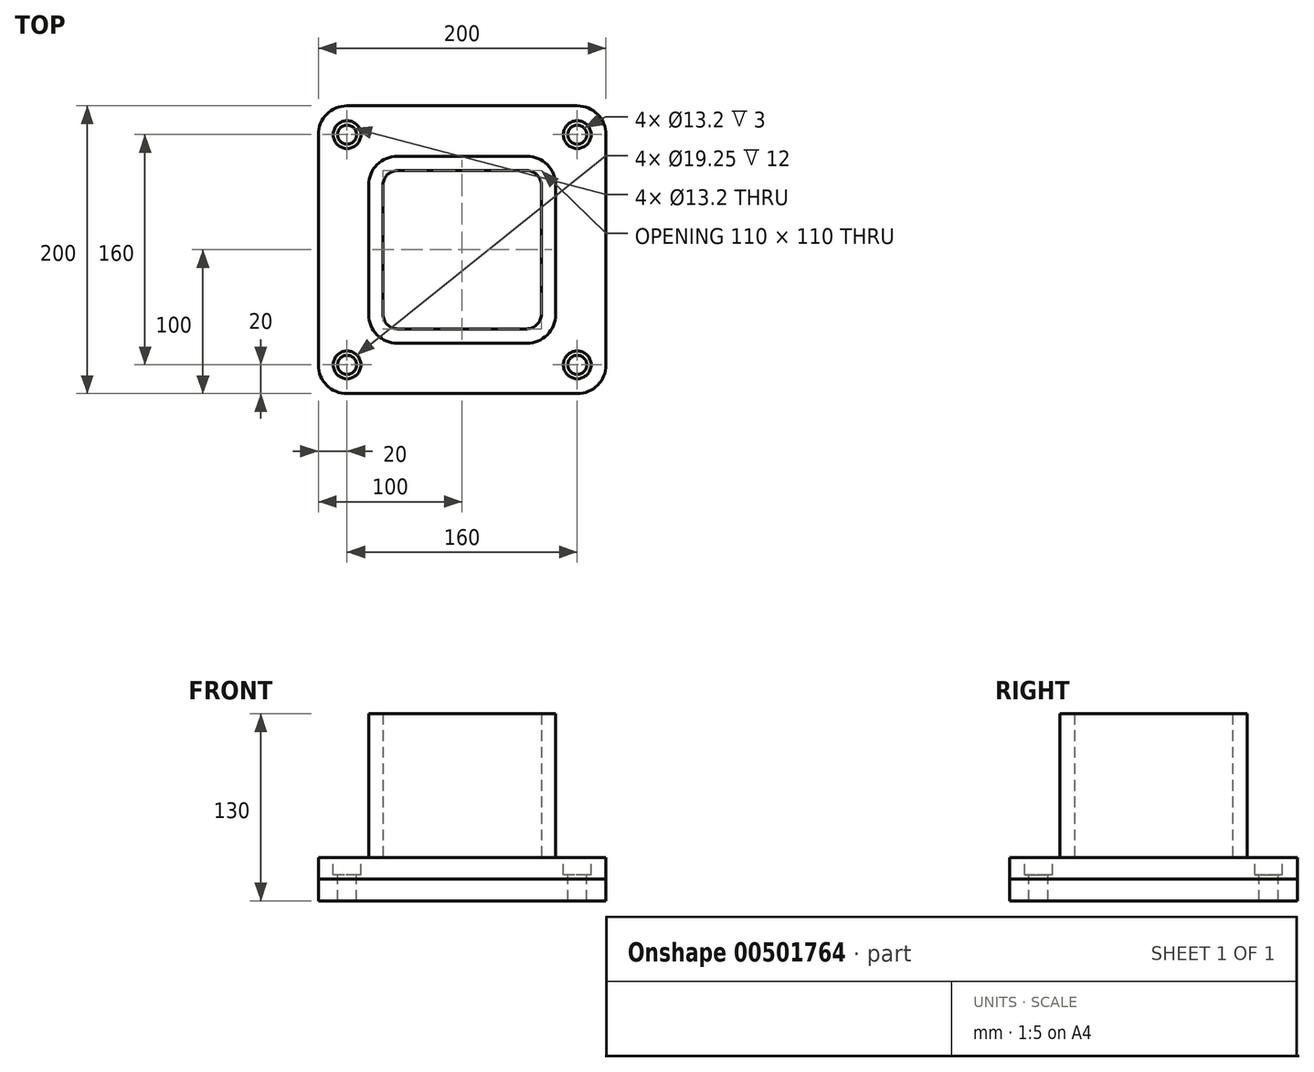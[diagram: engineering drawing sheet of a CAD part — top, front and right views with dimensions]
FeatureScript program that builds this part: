
annotation { "Feature Type Name" : "Feature", "Feature Type Description" : "" }
export const myFeature = defineFeature(function(context is Context, id is Id, definition is map)
    precondition{}
    {
        {
            var Q0;
            Q0=qCreatedBy(makeId("Top.planeOp"),FACE);
            var sketch = newSketch(context, id + "F0", { "sketchPlane" : qUnion([Q0])});
            skLineSegment(sketch, "E0.bottom", {"start": v(100, -100) * mm, "end": v(-100, -100) * mm});
            skLineSegment(sketch, "E0.top", {"start": v(100, 100) * mm, "end": v(-100, 100) * mm});
            skLineSegment(sketch, "E0.left", {"start": v(100, -100) * mm, "end": v(100, 100) * mm});
            skLineSegment(sketch, "E0.right", {"start": v(-100, -100) * mm, "end": v(-100, 100) * mm});
            skPoint(sketch, "E0.middle", {"position": v(0, 0) * mm});
            skSolve(sketch);
        }
        {
            var Q0;
            Q0=makeQuery(id+"F0.imprint","IMPRINT",FACE,{"disambiguationData":[TD([[makeQuery(id+"F0.imprint","IMPRINT",EDGE,{"derivedFrom":sQuery(id+"F0.wireOp",EDGE,"E0.bottom")}),-1.0]])]});
            extrude(context, id + "F1", {"entities" : qUnion([Q0]), "depth" : 15 * mm});
        }
        {
            var Q0;
            Q0=makeQuery(id+"F1.opExtrude","SWEPT_EDGE",EDGE,{"disambiguationData":[OSD([sQuery(id+"F0.wireOp",EDGE,"E0.bottom"),sQuery(id+"F0.wireOp",EDGE,"E0.left")])]});
            var Q1;
            Q1=makeQuery(id+"F1.opExtrude","SWEPT_EDGE",EDGE,{"disambiguationData":[OSD([sQuery(id+"F0.wireOp",EDGE,"E0.top"),sQuery(id+"F0.wireOp",EDGE,"E0.left")])]});
            var Q2;
            Q2=makeQuery(id+"F1.opExtrude","SWEPT_EDGE",EDGE,{"disambiguationData":[OSD([sQuery(id+"F0.wireOp",EDGE,"E0.bottom"),sQuery(id+"F0.wireOp",EDGE,"E0.right")])]});
            var Q3;
            Q3=makeQuery(id+"F1.opExtrude","SWEPT_EDGE",EDGE,{"disambiguationData":[OSD([sQuery(id+"F0.wireOp",EDGE,"E0.top"),sQuery(id+"F0.wireOp",EDGE,"E0.right")])]});
            fillet(context, id + "F2", {"entities" : qUnion([Q0, Q1, Q2, Q3]), "radius" : 20 * mm, "tangentPropagation" : true, "allowEdgeOverflow" : false});
        }
        {
            var Q0;
            Q0=makeQuery(id+"F1.opExtrude","CAP_FACE",FACE,{"disambiguationData":[OSD([sQuery(id+"F0.wireOp",EDGE,"E0.bottom"),sQuery(id+"F0.wireOp",EDGE,"E0.top"),sQuery(id+"F0.wireOp",EDGE,"E0.left"),sQuery(id+"F0.wireOp",EDGE,"E0.right")])],"isStart":false});
            var sketch = newSketch(context, id + "F3", { "sketchPlane" : qUnion([Q0])});
            skLineSegment(sketch, "E1.bottom", {"start": v(80, -80) * mm, "end": v(-80, -80) * mm});
            skLineSegment(sketch, "E1.top", {"start": v(80, 80) * mm, "end": v(-80, 80) * mm});
            skLineSegment(sketch, "E1.left", {"start": v(80, -80) * mm, "end": v(80, 80) * mm});
            skLineSegment(sketch, "E1.right", {"start": v(-80, -80) * mm, "end": v(-80, 80) * mm});
            skPoint(sketch, "E1.middle", {"position": v(0, 0) * mm});
            skArc(sketch, "E2.0", {"start": v(100, 80) * mm, "mid": v(94.14, 94.14) * mm, "end": v(80, 100) * mm});
            skSolve(sketch);
        }
        {
            var Q0;
            Q0=sQuery(id+"F3.wireOp",VERTEX,"E2.0.center");
            var Q1;
            Q1=sQuery(id+"F3.wireOp",VERTEX,"E1.right.end");
            var Q2;
            Q2=sQuery(id+"F3.wireOp",VERTEX,"E1.right.start");
            var Q3;
            Q3=sQuery(id+"F3.wireOp",VERTEX,"E1.left.start");
            var Q4;
            Q4=makeQuery(id+"F1.opExtrude","SWEPT_BODY",BODY,{"disambiguationData":[OSD([sQuery(id+"F0.wireOp",EDGE,"E0.bottom"),sQuery(id+"F0.wireOp",EDGE,"E0.top"),sQuery(id+"F0.wireOp",EDGE,"E0.left"),sQuery(id+"F0.wireOp",EDGE,"E0.right")])]});
            hole(context, id + "F4", {"style" : HoleStyle.SIMPLE, "endStyle" : HoleEndStyle.THROUGH, "holeDiameter" : 13.2 * mm, "isTappedThrough" : true, "tappedDepth" : 12.7 * mm, "tapClearance" : 3, "locations" : qUnion([Q0, Q1, Q2, Q3]), "scope" : qUnion([Q4])});
        }
        {
            var Q0;
            Q0=makeQuery(id+"F1.opExtrude","CAP_FACE",FACE,{"disambiguationData":[OSD([sQuery(id+"F0.wireOp",EDGE,"E0.bottom"),sQuery(id+"F0.wireOp",EDGE,"E0.top"),sQuery(id+"F0.wireOp",EDGE,"E0.left"),sQuery(id+"F0.wireOp",EDGE,"E0.right")])],"isStart":false});
            var sketch = newSketch(context, id + "F5", { "sketchPlane" : qUnion([Q0])});
            skLineSegment(sketch, "E3.0", {"start": v(-100, -80) * mm, "end": v(-100, 80) * mm});
            skArc(sketch, "E4.0", {"start": v(-100, -80) * mm, "mid": v(-94.14, -94.14) * mm, "end": v(-80, -100) * mm});
            skLineSegment(sketch, "E5.0", {"start": v(80, -100) * mm, "end": v(-80, -100) * mm});
            skArc(sketch, "E6.0", {"start": v(80, -100) * mm, "mid": v(94.14, -94.14) * mm, "end": v(100, -80) * mm});
            skLineSegment(sketch, "E7.0", {"start": v(100, -80) * mm, "end": v(100, 80) * mm});
            skArc(sketch, "E8.0", {"start": v(100, 80) * mm, "mid": v(94.14, 94.14) * mm, "end": v(80, 100) * mm});
            skLineSegment(sketch, "E9.0", {"start": v(80, 100) * mm, "end": v(-80, 100) * mm});
            skArc(sketch, "E10.0", {"start": v(-80, 100) * mm, "mid": v(-94.14, 94.14) * mm, "end": v(-100, 80) * mm});
            skSolve(sketch);
        }
        {
            var Q0;
            Q0 = qSketchRegion(id + "F5", true);
            extrude(context, id + "F6", {"entities" : qUnion([Q0]), "depth" : 15 * mm});
        }
        {
            var Q0;
            Q0=makeQuery(id+"F6.opExtrude","CAP_FACE",FACE,{"disambiguationData":[OSD([sQuery(id+"F5.wireOp",EDGE,"E3.0"),sQuery(id+"F5.wireOp",EDGE,"E4.0"),sQuery(id+"F5.wireOp",EDGE,"E5.0"),sQuery(id+"F5.wireOp",EDGE,"E6.0"),sQuery(id+"F5.wireOp",EDGE,"E7.0"),sQuery(id+"F5.wireOp",EDGE,"E8.0"),sQuery(id+"F5.wireOp",EDGE,"E9.0"),sQuery(id+"F5.wireOp",EDGE,"E10.0")])],"isStart":false});
            var sketch = newSketch(context, id + "F7", { "sketchPlane" : qUnion([Q0])});
            skPoint(sketch, "E11.0", {"position": v(-80, 80) * mm});
            skPoint(sketch, "E12.0", {"position": v(80, 80) * mm});
            skPoint(sketch, "E13.0", {"position": v(80, -80) * mm});
            skPoint(sketch, "E14.0", {"position": v(-80, -80) * mm});
            skSolve(sketch);
        }
        {
            var Q0;
            Q0=sQuery(id+"F7.wireOp",VERTEX,"E14.0");
            var Q1;
            Q1=sQuery(id+"F7.wireOp",VERTEX,"E11.0");
            var Q2;
            Q2=sQuery(id+"F7.wireOp",VERTEX,"E12.0");
            var Q3;
            Q3=sQuery(id+"F7.wireOp",VERTEX,"E13.0");
            var Q4;
            Q4=makeQuery(id+"F6.opExtrude","SWEPT_BODY",BODY,{"disambiguationData":[OSD([sQuery(id+"F5.wireOp",EDGE,"E3.0"),sQuery(id+"F5.wireOp",EDGE,"E4.0"),sQuery(id+"F5.wireOp",EDGE,"E5.0"),sQuery(id+"F5.wireOp",EDGE,"E6.0"),sQuery(id+"F5.wireOp",EDGE,"E7.0"),sQuery(id+"F5.wireOp",EDGE,"E8.0"),sQuery(id+"F5.wireOp",EDGE,"E9.0"),sQuery(id+"F5.wireOp",EDGE,"E10.0")])]});
            hole(context, id + "F8", {"style" : HoleStyle.C_BORE, "endStyle" : HoleEndStyle.THROUGH, "holeDiameter" : 13.2 * mm, "cBoreDiameter" : 19.25 * mm, "cBoreDepth" : 12 * mm, "isTappedThrough" : true, "tappedDepth" : 12.7 * mm, "tapClearance" : 3, "locations" : qUnion([Q0, Q1, Q2, Q3]), "scope" : qUnion([Q4])});
        }
        {
            var Q0;
            Q0=makeQuery(id+"F6.opExtrude","CAP_FACE",FACE,{"disambiguationData":[OSD([sQuery(id+"F5.wireOp",EDGE,"E3.0"),sQuery(id+"F5.wireOp",EDGE,"E4.0"),sQuery(id+"F5.wireOp",EDGE,"E5.0"),sQuery(id+"F5.wireOp",EDGE,"E6.0"),sQuery(id+"F5.wireOp",EDGE,"E7.0"),sQuery(id+"F5.wireOp",EDGE,"E8.0"),sQuery(id+"F5.wireOp",EDGE,"E9.0"),sQuery(id+"F5.wireOp",EDGE,"E10.0")])],"isStart":false});
            var sketch = newSketch(context, id + "F9", { "sketchPlane" : qUnion([Q0])});
            skLineSegment(sketch, "E15.bottom", {"start": v(45, -65) * mm, "end": v(-45, -65) * mm});
            skLineSegment(sketch, "E15.top", {"start": v(45, 65) * mm, "end": v(-45, 65) * mm});
            skLineSegment(sketch, "E15.left", {"start": v(65, -45) * mm, "end": v(65, 45) * mm});
            skLineSegment(sketch, "E15.right", {"start": v(-65, -45) * mm, "end": v(-65, 45) * mm});
            skPoint(sketch, "E15.middle", {"position": v(0, 0) * mm});
            skLineSegment(sketch, "E16.0", {"start": v(45, 55) * mm, "end": v(-45, 55) * mm});
            skLineSegment(sketch, "E16.1", {"start": v(55, -45) * mm, "end": v(55, 45) * mm});
            skLineSegment(sketch, "E16.2", {"start": v(45, -55) * mm, "end": v(-45, -55) * mm});
            skLineSegment(sketch, "E16.3", {"start": v(-55, -45) * mm, "end": v(-55, 45) * mm});
            skPoint(sketch, "E17.visualSharp", {"position": v(-55, 55) * mm});
            skArc(sketch, "E17.filletArc", {"start": v(-45, 55) * mm, "mid": v(-52.07, 52.07) * mm, "end": v(-55, 45) * mm});
            skPoint(sketch, "E18.visualSharp", {"position": v(-55, -55) * mm});
            skArc(sketch, "E18.filletArc", {"start": v(-55, -45) * mm, "mid": v(-52.07, -52.07) * mm, "end": v(-45, -55) * mm});
            skPoint(sketch, "E19.visualSharp", {"position": v(55, -55) * mm});
            skArc(sketch, "E19.filletArc", {"start": v(45, -55) * mm, "mid": v(52.07, -52.07) * mm, "end": v(55, -45) * mm});
            skPoint(sketch, "E20.visualSharp", {"position": v(55, 55) * mm});
            skArc(sketch, "E20.filletArc", {"start": v(55, 45) * mm, "mid": v(52.07, 52.07) * mm, "end": v(45, 55) * mm});
            skPoint(sketch, "E21.visualSharp", {"position": v(-65, 65) * mm});
            skArc(sketch, "E21.filletArc", {"start": v(-45, 65) * mm, "mid": v(-59.14, 59.14) * mm, "end": v(-65, 45) * mm});
            skPoint(sketch, "E22.visualSharp", {"position": v(65, 65) * mm});
            skArc(sketch, "E22.filletArc", {"start": v(65, 45) * mm, "mid": v(59.14, 59.14) * mm, "end": v(45, 65) * mm});
            skPoint(sketch, "E23.visualSharp", {"position": v(65, -65) * mm});
            skArc(sketch, "E23.filletArc", {"start": v(45, -65) * mm, "mid": v(59.14, -59.14) * mm, "end": v(65, -45) * mm});
            skPoint(sketch, "E24.visualSharp", {"position": v(-65, -65) * mm});
            skArc(sketch, "E24.filletArc", {"start": v(-65, -45) * mm, "mid": v(-59.14, -59.14) * mm, "end": v(-45, -65) * mm});
            skSolve(sketch);
        }
        {
            var Q0;
            Q0 = qSketchRegion(id + "F9", true);
            extrude(context, id + "F10", {"entities" : qUnion([Q0]), "depth" : 100 * mm});
        }
    });
